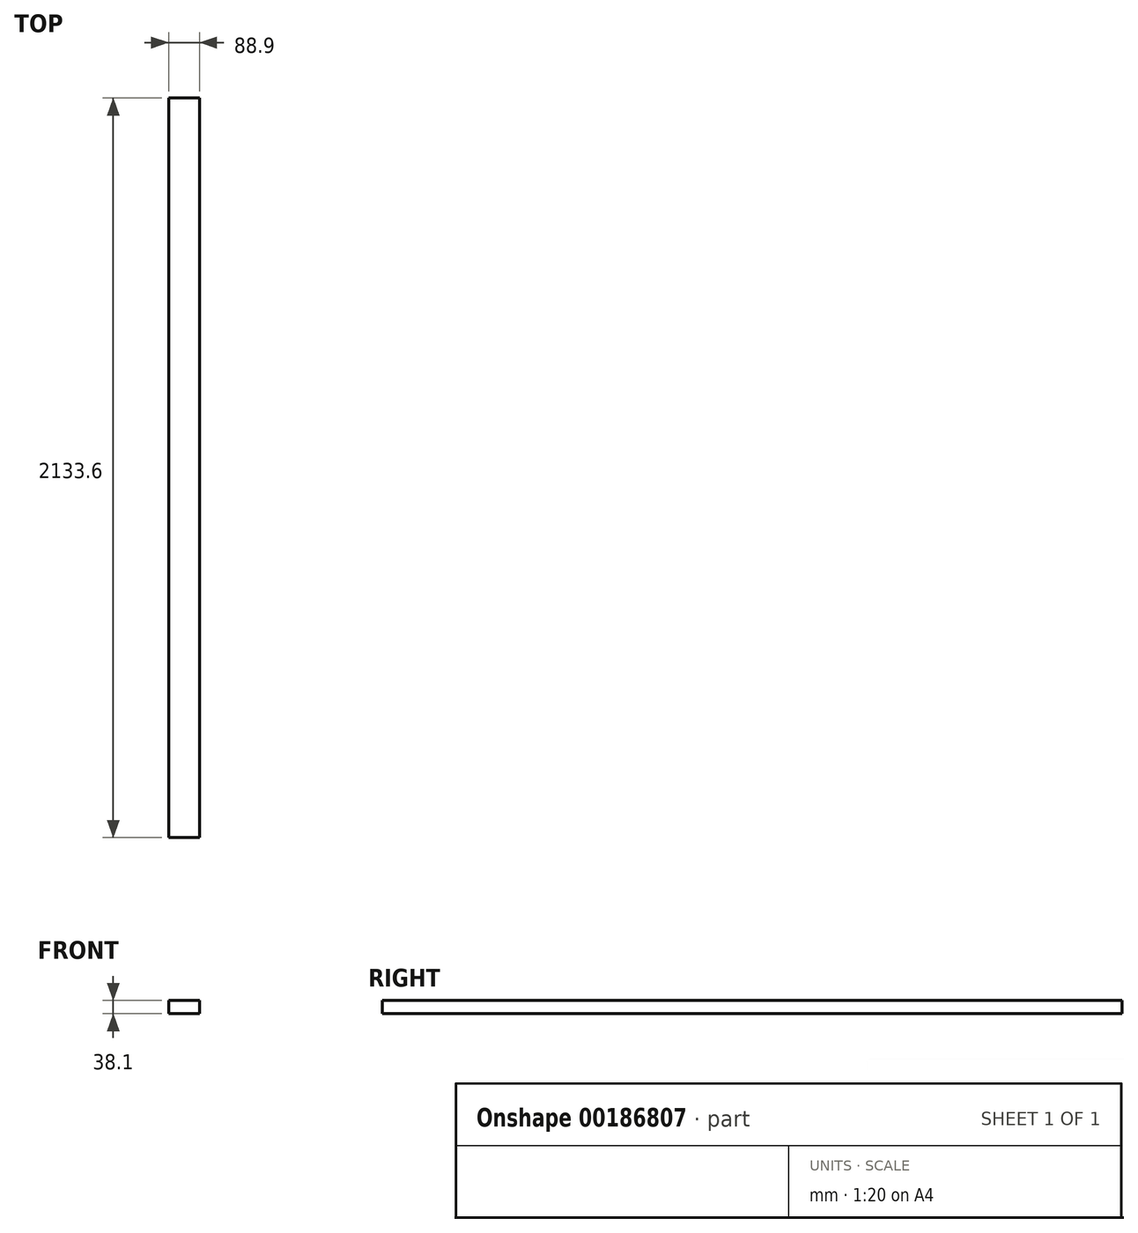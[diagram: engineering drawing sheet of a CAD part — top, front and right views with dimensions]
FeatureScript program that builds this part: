
annotation { "Feature Type Name" : "Feature", "Feature Type Description" : "" }
export const myFeature = defineFeature(function(context is Context, id is Id, definition is map)
    precondition{}
    {
        {
            var Q0;
            Q0=qCreatedBy(makeId("Front.planeOp"),FACE);
            var sketch = newSketch(context, id + "F0", { "sketchPlane" : qUnion([Q0])});
            skLineSegment(sketch, "E0.bottom", {"start": v(0, 0) * mm, "end": v(88.9, 0) * mm});
            skLineSegment(sketch, "E0.top", {"start": v(0, 38.1) * mm, "end": v(88.9, 38.1) * mm});
            skLineSegment(sketch, "E0.left", {"start": v(0, 0) * mm, "end": v(0, 38.1) * mm});
            skLineSegment(sketch, "E0.right", {"start": v(88.9, 0) * mm, "end": v(88.9, 38.1) * mm});
            skSolve(sketch);
        }
        {
            var Q0;
            Q0=makeQuery(id+"F0.imprint","IMPRINT",FACE,{"disambiguationData":[TD([[makeQuery(id+"F0.imprint","IMPRINT",EDGE,{"derivedFrom":sQuery(id+"F0.wireOp",EDGE,"E0.bottom")}),1.0]])]});
            extrude(context, id + "F1", {"entities" : qUnion([Q0]), "depth" : 2133.6 * mm});
        }
    });
